# Revit family: Elite_es24
name_source: partatom
category: Plumbing Fixtures
units: mm (PartAtom-declared; Revit-internal decimal feet)

## family parameters
Always vertical = Yes
Cut with Voids When Loaded = No
Part Type = Normal
Room Calculation Point = No
Round Connector Dimension = Use Diameter
Shared = No
Work Plane-Based = No

## types (3) — shared parameters
Design Country = Slovenia
Manufacturer Country = Slovenia
Manufacturer Name = HERZ/Unitas
Masterformat 2024 Code = 22 41 39
Masterformat 2024 Description = Residential Faucets, Supplies, and Trim
Material = Nickel chromium-plated
Product Family = Elite
Product Group = Kitchen mixer
UNSPSC Code = 3018
URL = https://www.herz-taps.com
Uniclass 2015 Code = Pr_40_20_87
Uniclass 2015 Name = Taps and water supply outlet fittings
Uniformat II Code = D2010
Uniformat II Description = Plumbing Fixtures
Website 1 = www.unitas.rs
Website 2 = www.herz.rs
Website 3 = www.herz.eu
zero-valued in all types: Default Elevation

## per-type parameters (varying)
| type | Black | Product Name | Product SKU | Red | White |
| es24_00123 | No | 00123 Elite Slim 24 | 00123 | Yes | No |
| es24_00124 | Yes | 00124 Elite Slim 24 | 00124 | No | No |
| es24_00125 | No | 00125 Elite Slim 24 | 00125 | No | Yes |

## geometry (parser evidence)
native form markers: Sweep x22
no freeform markers — native parametric forms only
